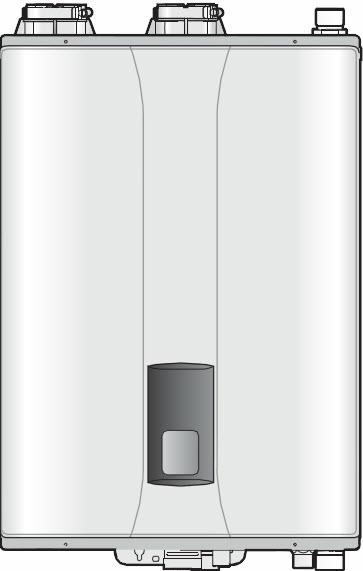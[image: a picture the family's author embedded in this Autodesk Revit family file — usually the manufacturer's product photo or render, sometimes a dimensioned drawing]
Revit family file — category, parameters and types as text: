
# Revit family: Water_Heater-Navien-NHB_Series
name_source: partatom
category: Mechanical Equipment
revit_build: Autodesk Revit MEP 2013 (Build: 20130531_2115(x64)
units: mm (PartAtom-declared; Revit-internal decimal feet)

## types (4) — shared parameters
Apparent Load = 0 VA
Cold Water Inlet = 1"
Default Elevation = 4' - 0"
Description = Condensing Gas Boiler (NHB)
Enclosure = Metal - Navien - White
Exhaust = 3"
Frequency = 60 Hz
Gas Inlet = 1"
Height = 2' - 0"
Hot Water Outlet = 1"
Intake = 3"
Manufacturer = Navien Inc.
Natural Gas Supply Pressure = 3.5 in.–10.5 in. WC
Number of Poles = 1
Phase = 1
Power Factor = 1
Product Documentation Link = http://us.navien.com
Product Name = NHB
Product Page URL = http://us.navien.com
Propane Gas Supply Pressure = 8.0 in.–13.5 in. WC
Recirculation Inlet = 0"
URL = http://us.navien.com
Voltage = 120 V
Width = 1' - 5"

## per-type parameters (varying)
| type | Heating Capacity | Length | Model | Operating Weight |
| NHB 055 | 51000.0 Btu/h | 1' - 0" | NHB - 055 | 73.00 lb |
| NHB 080 | 74000.0 Btu/h | 1' - 0" | NHB - 080 | 73.00 lb |
| NHB 110 | 102000.0 Btu/h | 1' - 1" | NHB - 110 | 80.00 lb |
| NHB 150 | 138000.0 Btu/h | 1' - 1" | NHB - 150 | 80.00 lb |

## geometry (parser evidence)
native form markers: Blend x4, Sweep x6
no freeform markers — native parametric forms only
